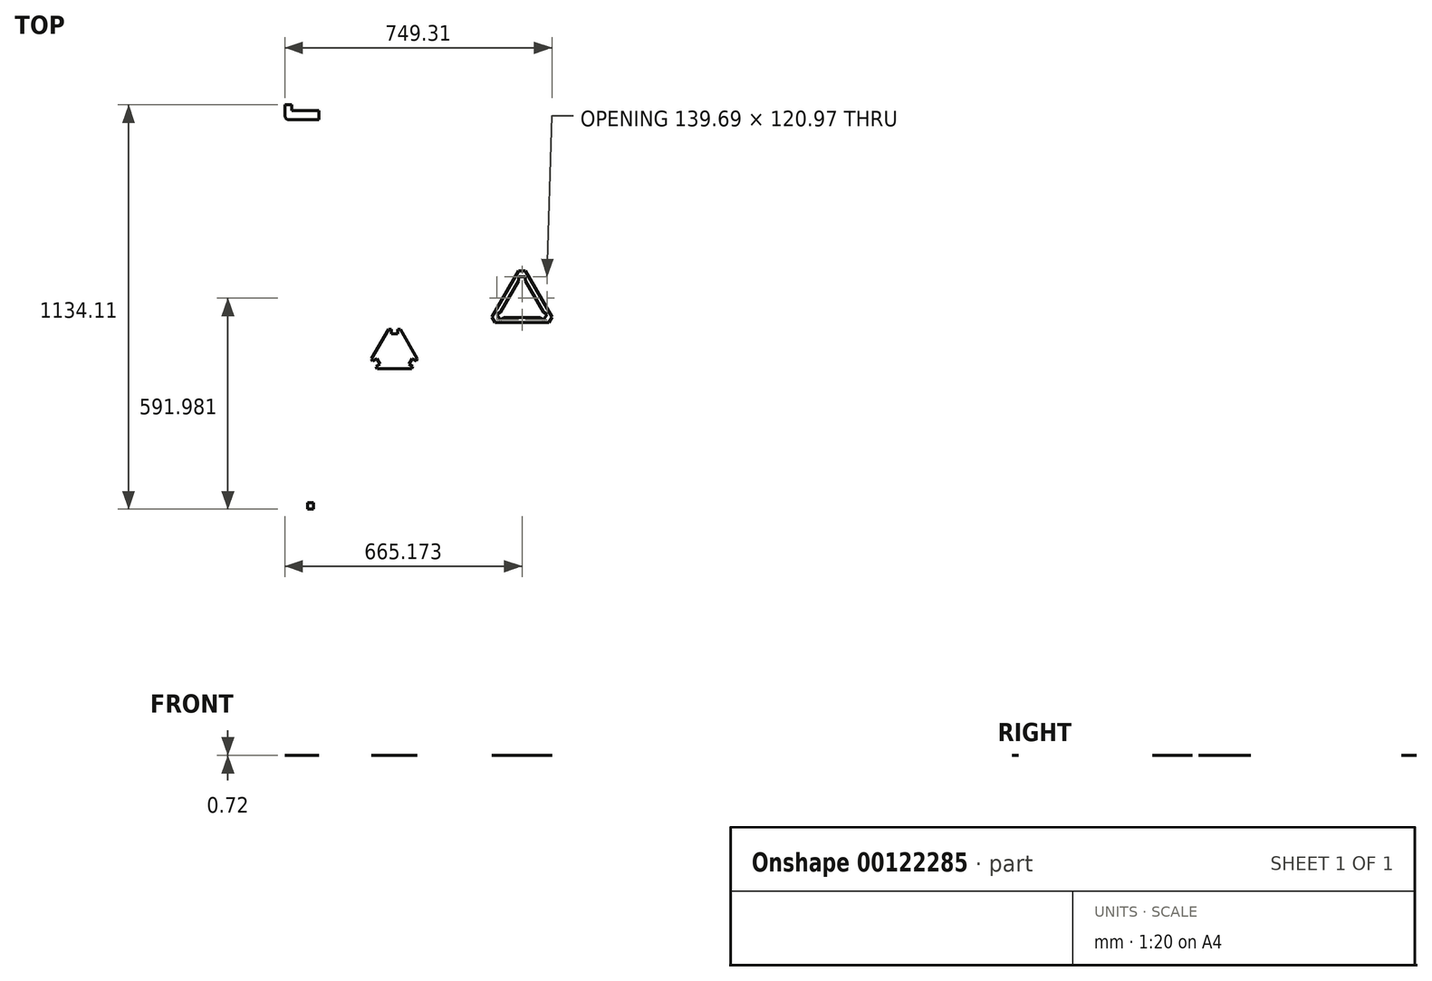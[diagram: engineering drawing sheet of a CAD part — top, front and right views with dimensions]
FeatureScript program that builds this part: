
annotation { "Feature Type Name" : "Feature", "Feature Type Description" : "" }
export const myFeature = defineFeature(function(context is Context, id is Id, definition is map)
    precondition{}
    {
        {
            assignVariable(context, id + "F0", {"name" : "ply34", "anyValue" : 0.72});
        }
        {
            var Q0;
            Q0=qCreatedBy(makeId("Top.planeOp"),FACE);
            var sketch = newSketch(context, id + "F1", { "sketchPlane" : qUnion([Q0])});
            skLineSegment(sketch, "E0.bottom", {"start": v(0, 0) * mm, "end": v(31.75, 0) * mm});
            skLineSegment(sketch, "E0.top", {"start": v(0, 711.2) * mm, "end": v(31.75, 711.2) * mm});
            skLineSegment(sketch, "E0.left", {"start": v(0, 0) * mm, "end": v(0, 711.2) * mm});
            skLineSegment(sketch, "E0.right", {"start": v(31.75, 0) * mm, "end": v(31.75, 711.2) * mm});
            skLineSegment(sketch, "E1.bottom", {"start": v(0, 0) * mm, "end": v(41.9, 0) * mm});
            skLineSegment(sketch, "E1.top", {"start": v(0, -406.4) * mm, "end": v(41.91, -406.4) * mm});
            skLineSegment(sketch, "E1.left", {"start": v(0, 0) * mm, "end": v(0, -406.4) * mm});
            skLineSegment(sketch, "E1.right", {"start": v(41.9, 0) * mm, "end": v(41.91, -406.4) * mm});
            skLineSegment(sketch, "E2.bottom", {"start": v(31.75, 711.2) * mm, "end": v(-44.45, 711.2) * mm});
            skLineSegment(sketch, "E2.top", {"start": v(31.75, 685.8) * mm, "end": v(-44.45, 685.8) * mm});
            skLineSegment(sketch, "E2.left", {"start": v(31.75, 711.2) * mm, "end": v(31.75, 685.8) * mm});
            skLineSegment(sketch, "E2.right", {"start": v(-44.45, 711.2) * mm, "end": v(-44.45, 685.8) * mm});
            skLineSegment(sketch, "E3.bottom", {"start": v(-44.45, 685.8) * mm, "end": v(-50.8, 685.8) * mm});
            skLineSegment(sketch, "E3.top", {"start": v(-44.45, 727.7) * mm, "end": v(-63.5, 727.7) * mm});
            skLineSegment(sketch, "E3.left", {"start": v(-44.45, 685.8) * mm, "end": v(-44.45, 727.7) * mm});
            skLineSegment(sketch, "E3.right", {"start": v(-63.5, 698.5) * mm, "end": v(-63.5, 727.7) * mm});
            skLineSegment(sketch, "E4.bottom", {"start": v(31.75, 711.2) * mm, "end": v(12.7, 711.2) * mm});
            skLineSegment(sketch, "E4.top", {"start": v(31.75, 727.7) * mm, "end": v(12.7, 727.7) * mm});
            skLineSegment(sketch, "E4.left", {"start": v(31.75, 711.2) * mm, "end": v(31.75, 727.7) * mm});
            skLineSegment(sketch, "E4.right", {"start": v(12.7, 711.2) * mm, "end": v(12.7, 727.7) * mm});
            skLineSegment(sketch, "E5.bottom", {"start": v(0, -406.4) * mm, "end": v(16.51, -406.4) * mm});
            skLineSegment(sketch, "E5.top", {"start": v(0, -388.11) * mm, "end": v(16.51, -388.11) * mm});
            skLineSegment(sketch, "E5.left", {"start": v(0, -406.4) * mm, "end": v(0, -388.11) * mm});
            skLineSegment(sketch, "E5.right", {"start": v(16.51, -406.4) * mm, "end": v(16.51, -388.11) * mm});
            skLineSegment(sketch, "E6.bottom", {"start": v(0, 431.8) * mm, "end": v(16.51, 431.8) * mm});
            skLineSegment(sketch, "E6.top", {"start": v(0, 413.51) * mm, "end": v(16.51, 413.51) * mm});
            skLineSegment(sketch, "E6.left", {"start": v(0, 431.8) * mm, "end": v(0, 413.51) * mm});
            skLineSegment(sketch, "E6.right", {"start": v(16.51, 431.8) * mm, "end": v(16.51, 413.51) * mm});
            skLineSegment(sketch, "E7.0", {"start": v(194.06, 15.84) * mm, "end": v(234.7, 86.23) * mm});
            skLineSegment(sketch, "E7.1", {"start": v(252.98, 86.23) * mm, "end": v(293.62, 15.84) * mm});
            skLineSegment(sketch, "E7.2", {"start": v(284.48, 0) * mm, "end": v(203.2, 0) * mm});
            skLineSegment(sketch, "E8", {"start": v(234.7, 86.23) * mm, "end": v(252.98, 86.23) * mm});
            skLineSegment(sketch, "E9", {"start": v(293.62, 15.84) * mm, "end": v(284.48, 0) * mm});
            skLineSegment(sketch, "E10", {"start": v(194.06, 15.84) * mm, "end": v(203.2, 0) * mm});
            skLineSegment(sketch, "E11.0", {"start": v(541.73, 146.65) * mm, "end": v(592.53, 234.64) * mm});
            skLineSegment(sketch, "E11.1", {"start": v(610.82, 234.64) * mm, "end": v(661.62, 146.65) * mm});
            skLineSegment(sketch, "E11.2", {"start": v(652.47, 130.81) * mm, "end": v(550.87, 130.81) * mm});
            skLineSegment(sketch, "E12", {"start": v(592.53, 234.64) * mm, "end": v(610.82, 234.64) * mm});
            skLineSegment(sketch, "E13", {"start": v(661.62, 146.65) * mm, "end": v(652.47, 130.81) * mm});
            skLineSegment(sketch, "E14", {"start": v(541.73, 146.65) * mm, "end": v(550.87, 130.81) * mm});
            skLineSegment(sketch, "E15.0", {"start": v(517.53, 132.68) * mm, "end": v(592.53, 262.58) * mm});
            skLineSegment(sketch, "E15.1", {"start": v(610.82, 262.58) * mm, "end": v(685.81, 132.68) * mm});
            skLineSegment(sketch, "E15.2", {"start": v(685.81, 132.68) * mm, "end": v(676.67, 116.84) * mm});
            skLineSegment(sketch, "E15.3", {"start": v(592.53, 262.58) * mm, "end": v(610.82, 262.58) * mm});
            skLineSegment(sketch, "E15.4", {"start": v(676.67, 116.84) * mm, "end": v(526.68, 116.84) * mm});
            skLineSegment(sketch, "E15.5", {"start": v(517.53, 132.68) * mm, "end": v(526.68, 116.84) * mm});
            skPoint(sketch, "E16", {"position": v(657.04, 138.73) * mm});
            skPoint(sketch, "E17", {"position": v(546.3, 138.73) * mm});
            skLineSegment(sketch, "E18", {"start": v(601.67, 234.64) * mm, "end": v(601.67, 130.81) * mm, "construction": true});
            skLineSegment(sketch, "E19", {"start": v(657.04, 138.73) * mm, "end": v(506.57, 225.6) * mm, "construction": true});
            skLineSegment(sketch, "E20", {"start": v(546.3, 138.73) * mm, "end": v(636.22, 190.64) * mm, "construction": true});
            skPoint(sketch, "E21", {"position": v(601.67, 272.41) * mm});
            skLineSegment(sketch, "E22.top", {"start": v(592.53, 246.07) * mm, "end": v(610.82, 246.07) * mm});
            skLineSegment(sketch, "E22.left", {"start": v(592.53, 234.64) * mm, "end": v(592.53, 246.07) * mm});
            skLineSegment(sketch, "E22.right", {"start": v(610.82, 234.64) * mm, "end": v(610.82, 246.07) * mm});
            skPoint(sketch, "E23", {"position": v(601.67, 170.7) * mm});
            skLineSegment(sketch, "E24.1.0", {"start": v(540.97, 125.1) * mm, "end": v(531.83, 140.93) * mm});
            skLineSegment(sketch, "E24.1.1", {"start": v(550.87, 130.8) * mm, "end": v(540.97, 125.1) * mm});
            skLineSegment(sketch, "E24.1.2", {"start": v(541.73, 146.65) * mm, "end": v(531.83, 140.93) * mm});
            skLineSegment(sketch, "E24.2.0", {"start": v(671.52, 140.93) * mm, "end": v(662.37, 125.1) * mm});
            skLineSegment(sketch, "E24.2.1", {"start": v(661.62, 146.65) * mm, "end": v(671.52, 140.93) * mm});
            skLineSegment(sketch, "E24.2.2", {"start": v(652.47, 130.81) * mm, "end": v(662.37, 125.1) * mm});
            skLineSegment(sketch, "E25.0", {"start": v(353.75, 386.14) * mm, "end": v(404.55, 474.13) * mm, "construction": true});
            skLineSegment(sketch, "E25.1", {"start": v(422.84, 474.13) * mm, "end": v(473.64, 386.14) * mm, "construction": true});
            skLineSegment(sketch, "E25.2", {"start": v(464.5, 370.3) * mm, "end": v(362.9, 370.3) * mm, "construction": true});
            skLineSegment(sketch, "E26", {"start": v(404.55, 474.13) * mm, "end": v(422.84, 474.13) * mm, "construction": true});
            skLineSegment(sketch, "E27.0", {"start": v(320.02, 386.14) * mm, "end": v(387.69, 503.34) * mm, "construction": true});
            skLineSegment(sketch, "E27.1", {"start": v(439.7, 503.34) * mm, "end": v(507.37, 386.14) * mm, "construction": true});
            skLineSegment(sketch, "E27.2", {"start": v(507.37, 386.14) * mm, "end": v(481.36, 341.1) * mm, "construction": true});
            skLineSegment(sketch, "E27.3", {"start": v(387.69, 503.34) * mm, "end": v(439.7, 503.34) * mm, "construction": true});
            skLineSegment(sketch, "E27.4", {"start": v(481.36, 341.1) * mm, "end": v(346.03, 341.1) * mm, "construction": true});
            skLineSegment(sketch, "E28", {"start": v(413.7, 474.13) * mm, "end": v(413.7, 370.3) * mm, "construction": true});
            skLineSegment(sketch, "E29", {"start": v(358.32, 378.22) * mm, "end": v(448.24, 430.13) * mm, "construction": true});
            skPoint(sketch, "E30", {"position": v(413.7, 489.9) * mm});
            skLineSegment(sketch, "E31.top", {"start": v(404.55, 486.83) * mm, "end": v(422.84, 486.83) * mm, "construction": true});
            skLineSegment(sketch, "E31.left", {"start": v(404.55, 474.13) * mm, "end": v(404.55, 486.83) * mm, "construction": true});
            skLineSegment(sketch, "E31.right", {"start": v(422.84, 474.13) * mm, "end": v(422.84, 486.83) * mm, "construction": true});
            skLineSegment(sketch, "E32.bottom", {"start": v(404.55, 499.53) * mm, "end": v(422.84, 499.53) * mm});
            skLineSegment(sketch, "E32.top", {"start": v(404.55, 461.43) * mm, "end": v(422.84, 461.43) * mm});
            skLineSegment(sketch, "E32.left", {"start": v(404.55, 499.53) * mm, "end": v(404.55, 461.43) * mm});
            skLineSegment(sketch, "E32.right", {"start": v(422.84, 499.53) * mm, "end": v(422.84, 461.43) * mm});
            skLineSegment(sketch, "E33.top", {"start": v(404.55, 448.73) * mm, "end": v(422.84, 448.73) * mm});
            skLineSegment(sketch, "E33.left", {"start": v(404.55, 499.53) * mm, "end": v(404.55, 448.73) * mm});
            skLineSegment(sketch, "E33.right", {"start": v(422.84, 499.53) * mm, "end": v(422.84, 448.73) * mm});
            skLineSegment(sketch, "E34.bottom", {"start": v(422.84, 499.53) * mm, "end": v(404.55, 499.53) * mm});
            skLineSegment(sketch, "E34.top", {"start": v(422.84, 486.83) * mm, "end": v(404.55, 486.83) * mm});
            skLineSegment(sketch, "E34.left", {"start": v(422.84, 499.53) * mm, "end": v(422.84, 486.83) * mm});
            skLineSegment(sketch, "E34.right", {"start": v(404.55, 499.53) * mm, "end": v(404.55, 486.83) * mm});
            skLineSegment(sketch, "E35.0", {"start": v(179.4, 15.84) * mm, "end": v(195.87, -12.7) * mm});
            skLineSegment(sketch, "E35.1", {"start": v(227.36, 98.93) * mm, "end": v(260.32, 98.93) * mm});
            skLineSegment(sketch, "E35.2", {"start": v(260.32, 98.93) * mm, "end": v(308.29, 15.84) * mm});
            skLineSegment(sketch, "E35.3", {"start": v(179.4, 15.84) * mm, "end": v(227.36, 98.93) * mm});
            skLineSegment(sketch, "E35.4", {"start": v(308.29, 15.84) * mm, "end": v(291.81, -12.7) * mm});
            skLineSegment(sketch, "E35.5", {"start": v(291.81, -12.7) * mm, "end": v(195.87, -12.7) * mm});
            skLineSegment(sketch, "E36", {"start": v(234.7, 86.23) * mm, "end": v(234.7, 98.93) * mm});
            skLineSegment(sketch, "E37", {"start": v(252.98, 86.23) * mm, "end": v(252.98, 98.93) * mm});
            skLineSegment(sketch, "E38", {"start": v(243.84, 86.23) * mm, "end": v(243.84, 0) * mm, "construction": true});
            skLineSegment(sketch, "E39", {"start": v(289.05, 7.92) * mm, "end": v(214.38, 51.03) * mm, "construction": true});
            skPoint(sketch, "E39.endSnap0", {"position": v(214.38, 51.03) * mm});
            skPoint(sketch, "E40", {"position": v(243.84, 34.02) * mm});
            skLineSegment(sketch, "E41.1.0", {"start": v(194.06, 15.84) * mm, "end": v(183.06, 9.49) * mm});
            skLineSegment(sketch, "E41.1.1", {"start": v(203.2, 0) * mm, "end": v(192.2, -6.35) * mm});
            skLineSegment(sketch, "E41.1.2", {"start": v(203.2, 0) * mm, "end": v(194.06, 15.84) * mm});
            skLineSegment(sketch, "E41.2.0", {"start": v(284.48, 0) * mm, "end": v(295.48, -6.35) * mm});
            skLineSegment(sketch, "E41.2.1", {"start": v(293.62, 15.84) * mm, "end": v(304.62, 9.49) * mm});
            skLineSegment(sketch, "E42", {"start": v(353.75, 386.14) * mm, "end": v(362.9, 370.3) * mm, "construction": true});
            skLineSegment(sketch, "E43", {"start": v(464.5, 370.3) * mm, "end": v(473.64, 386.14) * mm, "construction": true});
            skLineSegment(sketch, "E44", {"start": v(320.02, 386.14) * mm, "end": v(346.03, 341.1) * mm, "construction": true});
            skPoint(sketch, "E45", {"position": v(413.7, 410.19) * mm});
            skLineSegment(sketch, "E46.1.0", {"start": v(384.9, 383) * mm, "end": v(375.75, 398.84) * mm});
            skLineSegment(sketch, "E46.1.1", {"start": v(362.9, 370.3) * mm, "end": v(353.75, 386.14) * mm, "construction": true});
            skLineSegment(sketch, "E46.1.2", {"start": v(340.9, 357.6) * mm, "end": v(331.75, 373.44) * mm});
            skLineSegment(sketch, "E46.1.3", {"start": v(340.9, 357.6) * mm, "end": v(351.9, 363.95) * mm});
            skLineSegment(sketch, "E46.1.4", {"start": v(331.75, 373.44) * mm, "end": v(364.75, 392.49) * mm});
            skLineSegment(sketch, "E46.1.5", {"start": v(373.9, 376.65) * mm, "end": v(364.75, 392.49) * mm});
            skLineSegment(sketch, "E46.1.6", {"start": v(351.9, 363.95) * mm, "end": v(342.75, 379.79) * mm, "construction": true});
            skLineSegment(sketch, "E46.1.7", {"start": v(340.9, 357.6) * mm, "end": v(373.9, 376.65) * mm});
            skLineSegment(sketch, "E46.1.8", {"start": v(340.9, 357.6) * mm, "end": v(384.9, 383) * mm});
            skLineSegment(sketch, "E46.1.9", {"start": v(353.75, 386.14) * mm, "end": v(342.75, 379.79) * mm, "construction": true});
            skLineSegment(sketch, "E46.1.10", {"start": v(331.75, 373.44) * mm, "end": v(375.75, 398.84) * mm});
            skLineSegment(sketch, "E46.1.11", {"start": v(362.9, 370.3) * mm, "end": v(351.9, 363.95) * mm, "construction": true});
            skPoint(sketch, "E46.1.12", {"position": v(344.66, 370.33) * mm});
            skLineSegment(sketch, "E46.1.13", {"start": v(342.75, 379.79) * mm, "end": v(351.9, 363.95) * mm});
            skLineSegment(sketch, "E46.1.14", {"start": v(331.75, 373.44) * mm, "end": v(342.75, 379.79) * mm});
            skLineSegment(sketch, "E46.1.15", {"start": v(331.75, 373.44) * mm, "end": v(340.9, 357.6) * mm});
            skLineSegment(sketch, "E46.1.16", {"start": v(362.9, 370.3) * mm, "end": v(353.75, 386.14) * mm, "construction": true});
            skLineSegment(sketch, "E46.1.17", {"start": v(340.9, 357.6) * mm, "end": v(331.75, 373.44) * mm});
            skLineSegment(sketch, "E46.2.0", {"start": v(451.64, 398.84) * mm, "end": v(442.5, 383) * mm});
            skLineSegment(sketch, "E46.2.1", {"start": v(473.64, 386.14) * mm, "end": v(464.5, 370.3) * mm, "construction": true});
            skLineSegment(sketch, "E46.2.2", {"start": v(495.63, 373.44) * mm, "end": v(486.5, 357.6) * mm});
            skLineSegment(sketch, "E46.2.3", {"start": v(495.63, 373.44) * mm, "end": v(484.64, 379.79) * mm});
            skLineSegment(sketch, "E46.2.4", {"start": v(486.5, 357.6) * mm, "end": v(453.5, 376.65) * mm});
            skLineSegment(sketch, "E46.2.5", {"start": v(462.64, 392.49) * mm, "end": v(453.5, 376.65) * mm});
            skLineSegment(sketch, "E46.2.6", {"start": v(484.64, 379.79) * mm, "end": v(475.5, 363.95) * mm, "construction": true});
            skLineSegment(sketch, "E46.2.7", {"start": v(495.63, 373.44) * mm, "end": v(462.64, 392.49) * mm});
            skLineSegment(sketch, "E46.2.8", {"start": v(495.63, 373.44) * mm, "end": v(451.64, 398.84) * mm});
            skLineSegment(sketch, "E46.2.9", {"start": v(464.5, 370.3) * mm, "end": v(475.5, 363.95) * mm, "construction": true});
            skLineSegment(sketch, "E46.2.10", {"start": v(486.5, 357.6) * mm, "end": v(442.5, 383) * mm});
            skLineSegment(sketch, "E46.2.11", {"start": v(473.64, 386.14) * mm, "end": v(484.64, 379.79) * mm, "construction": true});
            skPoint(sketch, "E46.2.12", {"position": v(482.73, 370.33) * mm});
            skLineSegment(sketch, "E46.2.13", {"start": v(475.5, 363.95) * mm, "end": v(484.64, 379.79) * mm});
            skLineSegment(sketch, "E46.2.14", {"start": v(486.5, 357.6) * mm, "end": v(475.5, 363.95) * mm});
            skLineSegment(sketch, "E46.2.15", {"start": v(486.5, 357.6) * mm, "end": v(495.63, 373.44) * mm});
            skLineSegment(sketch, "E46.2.16", {"start": v(473.64, 386.14) * mm, "end": v(464.5, 370.3) * mm, "construction": true});
            skLineSegment(sketch, "E46.2.17", {"start": v(495.63, 373.44) * mm, "end": v(486.5, 357.6) * mm});
            skPoint(sketch, "E47", {"position": v(601.67, 116.84) * mm});
            skPoint(sketch, "E48", {"position": v(601.67, 262.58) * mm});
            skPoint(sketch, "E49", {"position": v(601.67, 246.07) * mm});
            skLineSegment(sketch, "E50", {"start": v(41.91, -406.4) * mm, "end": v(41.91, -711.2) * mm, "construction": true});
            skLineSegment(sketch, "E51", {"start": v(0, -406.4) * mm, "end": v(0, -711.2) * mm, "construction": true});
            skLineSegment(sketch, "E52", {"start": v(41.91, -457.2) * mm, "end": v(0, -457.2) * mm, "construction": true});
            skLineSegment(sketch, "E53", {"start": v(-50.8, -711.2) * mm, "end": v(-8.89, -711.2) * mm});
            skPoint(sketch, "E54.visualSharp", {"position": v(-63.5, 685.8) * mm});
            skArc(sketch, "E54.filletArc", {"start": v(-63.5, 698.5) * mm, "mid": v(-59.78, 689.52) * mm, "end": v(-50.8, 685.8) * mm});
            skFitSpline(sketch, "E55", {"points": [v(41.91, -406.4) * mm, v(-8.89, -711.2) * mm], "startDerivative": vector(0, -323.16) * mm, "endDerivative": vector(-152.4, -296.72) * mm});
            skFitSpline(sketch, "E56.0", {"points": [v(0, -406.4) * mm, v(0, -419.86) * mm, v(0, -446.3) * mm, v(-0.59, -484.5) * mm, v(-2.3, -521.37) * mm, v(-5.67, -557.04) * mm, v(-11.16, -591.66) * mm, v(-19.27, -625.48) * mm, v(-30.5, -658.8) * mm, v(-40.46, -680.94) * mm, v(-46.17, -692.05) * mm]});
            skSolve(sketch);
        }
        {
            var Q0;
            {var subQ3=sQuery(id+"F1.wireOp",EDGE,"E0.right");Q0=makeQuery(id+"F1.imprint","IMPRINT",FACE,{"disambiguationData":[TD([[makeQuery(id+"F1.imprint","IMPRINT",EDGE,{"derivedFrom":subQ3}),1.0]])]});}
            var Q1;
            Q1=makeQuery(id+"F1.imprint","IMPRINT",FACE,{"disambiguationData":[TD([[makeQuery(id+"F1.imprint","IMPRINT",EDGE,{"derivedFrom":sQuery(id+"F1.wireOp",EDGE,"E1.top")}),1.0]])]});
            var Q2;
            Q2=makeQuery(id+"F1.imprint","IMPRINT",FACE,{"disambiguationData":[TD([[makeQuery(id+"F1.imprint","IMPRINT",EDGE,{"derivedFrom":sQuery(id+"F1.wireOp",EDGE,"E1.top")}),-1.0]])]});
            var Q3;
            {var subQ3=sQuery(id+"F1.wireOp",EDGE,"E3.bottom");Q3=makeQuery(id+"F1.imprint","IMPRINT",FACE,{"disambiguationData":[TD([[makeQuery(id+"F1.imprint","IMPRINT",EDGE,{"derivedFrom":subQ3}),-1.0]])]});}
            var Q4;
            {var subQ0=sQuery(id+"F1.wireOp",EDGE,"E2.left");Q4=makeQuery(id+"F1.imprint","IMPRINT",FACE,{"disambiguationData":[TD([[makeQuery(id+"F1.imprint","IMPRINT",EDGE,{"derivedFrom":subQ0}),-1.0]])]});}
            var Q5;
            {var subQ0=sQuery(id+"F1.wireOp",EDGE,"E2.bottom");var subQ1=sQuery(id+"F1.wireOp",EDGE,"E0.left");var subQ2=makeQuery(id+"F1.imprint","INTERSECT",VERTEX,{"derivedFrom":[subQ1,subQ0]});Q5=makeQuery(id+"F1.imprint","IMPRINT",FACE,{"disambiguationData":[TD([[makeQuery(id+"F1.imprint","IMPRINT",EDGE,{"disambiguationData":[TD([[subQ2,1.0]])],"derivedFrom":subQ1}),1.0]])]});}
            var Q6;
            Q6=makeQuery(id+"F1.imprint","IMPRINT",FACE,{"disambiguationData":[TD([[makeQuery(id+"F1.imprint","IMPRINT",EDGE,{"derivedFrom":sQuery(id+"F1.wireOp",EDGE,"E7.1")}),1.0]])]});
            var Q7;
            Q7=makeQuery(id+"F1.imprint","IMPRINT",FACE,{"disambiguationData":[TD([[makeQuery(id+"F1.imprint","IMPRINT",EDGE,{"derivedFrom":sQuery(id+"F1.wireOp",EDGE,"E7.0")}),-1.0]])]});
            var Q8;
            Q8=makeQuery(id+"F1.imprint","IMPRINT",FACE,{"disambiguationData":[TD([[makeQuery(id+"F1.imprint","IMPRINT",EDGE,{"derivedFrom":sQuery(id+"F1.wireOp",EDGE,"E7.2")}),1.0]])]});
            var Q9;
            Q9=makeQuery(id+"F1.imprint","IMPRINT",FACE,{"disambiguationData":[TD([[makeQuery(id+"F1.imprint","IMPRINT",EDGE,{"derivedFrom":sQuery(id+"F1.wireOp",EDGE,"E7.0")}),1.0]])]});
            var Q10;
            Q10=makeQuery(id+"F1.imprint","IMPRINT",FACE,{"disambiguationData":[TD([[makeQuery(id+"F1.imprint","IMPRINT",EDGE,{"derivedFrom":sQuery(id+"F1.wireOp",EDGE,"E11.0")}),1.0]])]});
            extrude(context, id + "F2", {"entities" : qUnion([Q0, Q1, Q2, Q3, Q4, Q5, Q6, Q7, Q8, Q9, Q10]), "depth" : (getVariable(context, 'ply34')) * mm});
        }
    });
